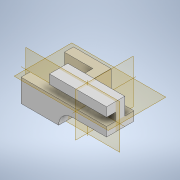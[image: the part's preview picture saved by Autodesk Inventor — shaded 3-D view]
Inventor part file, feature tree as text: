
AUTODESK INVENTOR PART (.ipt)
format: ipt  version: 2022.4 (Build 264492010, 492A)  size: 165,376 bytes
history: native  units: mm
features: extrude x4, sketch x3
ambient origin geometry x8: Origin, YZ Plane, XZ Plane, XY Plane, X Axis, Y Axis, Z Axis, Center Point
bodies: Solid1 (feature_tree)
feature tree (7):
  extrude  "Extrusion1"  Depth=3.0mm
  extrude  "Extrusion2"  Depth=1.6mm
  sketch  "Sketch4"  dims[d3=3.2mm d4=1.6mm]
  extrude  "Extrusion3"  Depth=1.6mm
  extrude  "Extrusion4"  Depth=1.6mm
  sketch  "Sketch3"  dims[d1=6.0mm d2=3.0mm]
  sketch  "Sketch6"  dims[d6=4.0mm d7=1.6mm d8=1.4mm d10=10.0mm d11=0.0mm d12=1.6mm d14=1.6mm d15=1.6mm d17=2.4mm d18=0.0mm d19=0.0mm d20=1.6mm d21=1.6mm d22=5.0mm d23=0.0mm d24=1.6mm d25=1.6mm d26=1.6mm d27=0.0mm d28=0.0mm]
